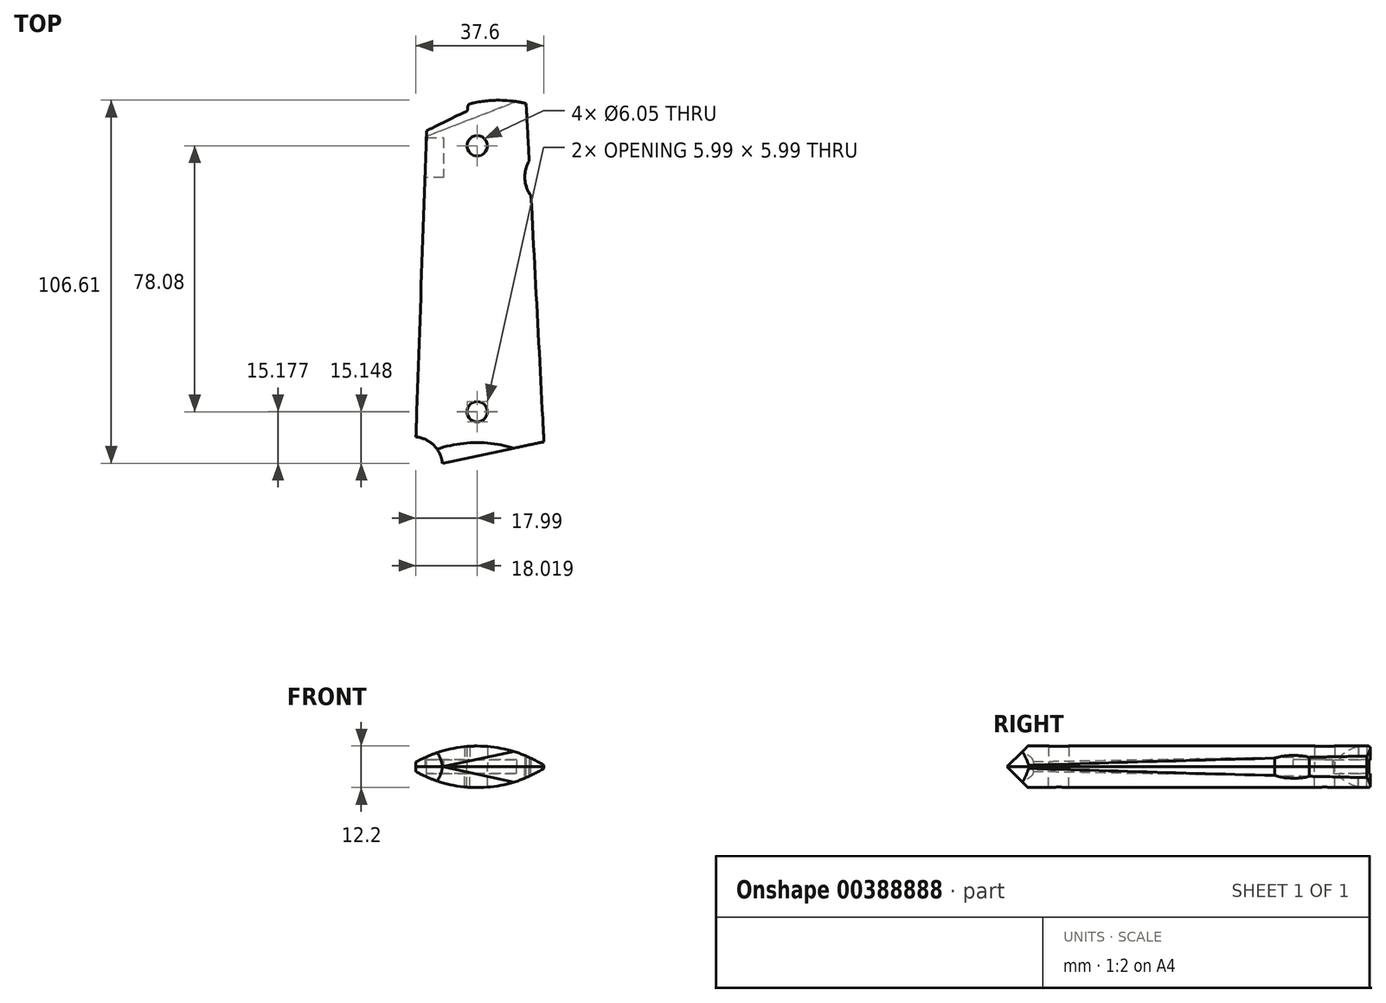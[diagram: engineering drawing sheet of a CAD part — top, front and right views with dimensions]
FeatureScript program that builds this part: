
annotation { "Feature Type Name" : "Feature", "Feature Type Description" : "" }
export const myFeature = defineFeature(function(context is Context, id is Id, definition is map)
    precondition{}
    {
        {
            var Q0;
            Q0=qCreatedBy(makeId("Top.planeOp"),FACE);
            var sketch = newSketch(context, id + "F0", { "sketchPlane" : qUnion([Q0])});
            skCircle(sketch, "E0", {"center": v(0, 44.02) * mm, "radius": 3.02 * mm});
            skCircle(sketch, "E1", {"center": v(0, -34.06) * mm, "radius": 3.02 * mm});
            skArc(sketch, "E2", {"start": v(-10.2, -49.21) * mm, "mid": v(-16.67, -41.7) * mm, "end": v(-25.95, -45.22) * mm});
            skArc(sketch, "E3", {"start": v(15.27, 39.57) * mm, "mid": v(13.98, 34.4) * mm, "end": v(15.8, 29.38) * mm});
            skArc(sketch, "E4", {"start": v(-14.98, 45) * mm, "mid": v(-15, 44.54) * mm, "end": v(-15.01, 44.08) * mm});
            skArc(sketch, "E5", {"start": v(-17.7, -32.88) * mm, "mid": v(-17.72, -33.47) * mm, "end": v(-17.73, -34.06) * mm});
            skLineSegment(sketch, "E6", {"start": v(15.2, 40.98) * mm, "end": v(15.27, 39.57) * mm});
            skLineSegment(sketch, "E7", {"start": v(-15.01, 44.08) * mm, "end": v(-17.73, -34) * mm});
            skLineSegment(sketch, "E8.trimOffspring", {"start": v(15.8, 29.38) * mm, "end": v(19.25, -36.1) * mm});
            skLineSegment(sketch, "E9", {"start": v(19.61, -42.88) * mm, "end": v(-10.2, -49.21) * mm});
            skLineSegment(sketch, "E10", {"start": v(0, -34.06) * mm, "end": v(-82.75, -34.06) * mm, "construction": true});
            skLineSegment(sketch, "E11", {"start": v(19.25, -36.1) * mm, "end": v(19.61, -42.88) * mm});
            skLineSegment(sketch, "E12", {"start": v(-17.73, -34) * mm, "end": v(-17.99, -41.47) * mm});
            skArc(sketch, "E13", {"start": v(14.38, 56.45) * mm, "mid": v(-0.93, 56.62) * mm, "end": v(-14.8, 50.16) * mm});
            skLineSegment(sketch, "E14", {"start": v(15.2, 40.98) * mm, "end": v(14.38, 56.45) * mm});
            skLineSegment(sketch, "E15", {"start": v(-15.01, 44.08) * mm, "end": v(-14.8, 50.16) * mm});
            skSolve(sketch);
        }
        {
            var Q0;
            Q0=makeQuery(id+"F0.imprint","IMPRINT",FACE,{"disambiguationData":[TD([[makeQuery(id+"F0.imprint","IMPRINT",EDGE,{"derivedFrom":sQuery(id+"F0.wireOp",EDGE,"E0")}),-1.0]])]});
            extrude(context, id + "F1", {"entities" : qUnion([Q0]), "depth" : 6.1 * mm});
        }
        {
            var Q0;
            Q0=qCreatedBy(makeId("Front.planeOp"),FACE);
            var sketch = newSketch(context, id + "F2", { "sketchPlane" : qUnion([Q0])});
            skCircle(sketch, "E16", {"center": v(0, -30.73) * mm, "radius": 36.83 * mm});
            skCircle(sketch, "E17", {"center": v(0, -30.73) * mm, "radius": 42.83 * mm});
            skSolve(sketch);
        }
        {
            var Q0;
            Q0=makeQuery(id+"F2.imprint","IMPRINT",FACE,{"disambiguationData":[TD([[makeQuery(id+"F2.imprint","IMPRINT",EDGE,{"derivedFrom":sQuery(id+"F2.wireOp",EDGE,"E16")}),-1.0]])]});
            extrude(context, id + "F3", {"entities" : qUnion([Q0]), "operationType" : NewBodyOperationType.REMOVE, "endBound" : BoundingType.SYMMETRIC, "depth" : 127 * mm});
        }
        {
            var Q0;
            Q0=qCreatedBy(makeId("Right.planeOp"),FACE);
            var sketch = newSketch(context, id + "F4", { "sketchPlane" : qUnion([Q0])});
            skLineSegment(sketch, "E18.0", {"start": v(-49.21, 4.65) * mm, "end": v(-49.21, 0) * mm});
            skLineSegment(sketch, "E18.1", {"start": v(-49.21, 0) * mm, "end": v(-41.47, 0) * mm});
            skLineSegment(sketch, "E19", {"start": v(-41.47, 0) * mm, "end": v(-57, 0) * mm});
            skLineSegment(sketch, "E20", {"start": v(-49.21, 0) * mm, "end": v(-41.47, 7.75) * mm});
            skLineSegment(sketch, "E21", {"start": v(-41.47, 7.75) * mm, "end": v(-52.4, 7.75) * mm});
            skLineSegment(sketch, "E22", {"start": v(-52.4, 7.75) * mm, "end": v(-52.4, 0) * mm});
            skSolve(sketch);
        }
        {
            var Q0;
            {var subQ0=sQuery(id+"F4.wireOp",EDGE,"E20");Q0=makeQuery(id+"F4.imprint","IMPRINT",FACE,{"disambiguationData":[TD([[makeQuery(id+"F4.imprint","IMPRINT",EDGE,{"derivedFrom":subQ0}),1.0]])]});}
            extrude(context, id + "F5", {"entities" : qUnion([Q0]), "operationType" : NewBodyOperationType.REMOVE, "endBound" : BoundingType.SYMMETRIC, "oppositeDirection" : true, "depth" : 76.2 * mm});
        }
        {
            var Q0;
            Q0=qCreatedBy(makeId("Top.planeOp"),FACE);
            var sketch = newSketch(context, id + "F6", { "sketchPlane" : qUnion([Q0])});
            skLineSegment(sketch, "E23", {"start": v(-14.86, 48.44) * mm, "end": v(-14.8, 50.16) * mm});
            skArc(sketch, "E24", {"start": v(-2.14, 56.34) * mm, "mid": v(-2.57, 56) * mm, "end": v(-2.77, 55.49) * mm});
            skLineSegment(sketch, "E25", {"start": v(-2.77, 55.49) * mm, "end": v(-2.85, 54.6) * mm});
            skArc(sketch, "E26", {"start": v(-3.68, 53.93) * mm, "mid": v(-3.12, 54.09) * mm, "end": v(-2.85, 54.6) * mm});
            skLineSegment(sketch, "E27", {"start": v(-3.68, 53.93) * mm, "end": v(-14.86, 48.44) * mm});
            skArc(sketch, "E28", {"start": v(-2.14, 56.34) * mm, "mid": v(-8.78, 53.9) * mm, "end": v(-14.8, 50.16) * mm});
            skLineSegment(sketch, "E29", {"start": v(-2.14, 56.34) * mm, "end": v(-2.14, 57.7) * mm});
            skLineSegment(sketch, "E30", {"start": v(-2.14, 57.7) * mm, "end": v(-16, 52.43) * mm});
            skLineSegment(sketch, "E31", {"start": v(-16, 52.43) * mm, "end": v(-14.86, 48.44) * mm});
            skSolve(sketch);
        }
        {
            var Q0;
            Q0=makeQuery(id+"F6.imprint","IMPRINT",FACE,{"disambiguationData":[TD([[makeQuery(id+"F6.imprint","IMPRINT",EDGE,{"derivedFrom":sQuery(id+"F6.wireOp",EDGE,"E23")}),-1.0]])]});
            var Q1;
            Q1=makeQuery(id+"F6.imprint","IMPRINT",FACE,{"disambiguationData":[TD([[makeQuery(id+"F6.imprint","IMPRINT",EDGE,{"derivedFrom":sQuery(id+"F6.wireOp",EDGE,"E23")}),1.0]])]});
            extrude(context, id + "F7", {"entities" : qUnion([Q0, Q1]), "operationType" : NewBodyOperationType.REMOVE, "depth" : 10.16 * mm});
        }
        {
            var Q0;
            Q0=makeQuery(id+"F1.opExtrude","SWEPT_BODY",BODY,{"disambiguationData":[OSD([sQuery(id+"F0.wireOp",EDGE,"E0"),sQuery(id+"F0.wireOp",EDGE,"E1"),sQuery(id+"F0.wireOp",EDGE,"E2"),sQuery(id+"F0.wireOp",EDGE,"E3"),sQuery(id+"F0.wireOp",EDGE,"E6"),sQuery(id+"F0.wireOp",EDGE,"E7"),sQuery(id+"F0.wireOp",EDGE,"E8.trimOffspring"),sQuery(id+"F0.wireOp",EDGE,"E9"),sQuery(id+"F0.wireOp",EDGE,"E11"),sQuery(id+"F0.wireOp",EDGE,"E12"),sQuery(id+"F0.wireOp",EDGE,"E13"),sQuery(id+"F0.wireOp",EDGE,"E14"),sQuery(id+"F0.wireOp",EDGE,"E15")])]});
            var Q1;
            Q1=qCreatedBy(makeId("Top.planeOp"),FACE);
            mirror(context, id + "F8", {"entities" : qUnion([Q0]), "mirrorPlane" : qUnion([Q1])});
        }
        {
            var Q0;
            Q0=makeQuery(id+"F1.opExtrude","CAP_FACE",FACE,{"disambiguationData":[OSD([sQuery(id+"F0.wireOp",EDGE,"E0"),sQuery(id+"F0.wireOp",EDGE,"E1"),sQuery(id+"F0.wireOp",EDGE,"E2"),sQuery(id+"F0.wireOp",EDGE,"E3"),sQuery(id+"F0.wireOp",EDGE,"E6"),sQuery(id+"F0.wireOp",EDGE,"E7"),sQuery(id+"F0.wireOp",EDGE,"E8.trimOffspring"),sQuery(id+"F0.wireOp",EDGE,"E9"),sQuery(id+"F0.wireOp",EDGE,"E11"),sQuery(id+"F0.wireOp",EDGE,"E12"),sQuery(id+"F0.wireOp",EDGE,"E13"),sQuery(id+"F0.wireOp",EDGE,"E14"),sQuery(id+"F0.wireOp",EDGE,"E15")])],"isStart":true});
            var sketch = newSketch(context, id + "F9", { "sketchPlane" : qUnion([Q0])});
            skLineSegment(sketch, "E32", {"start": v(-14.93, -46.4) * mm, "end": v(-9.85, -46.4) * mm});
            skLineSegment(sketch, "E33", {"start": v(-9.85, -46.4) * mm, "end": v(-9.85, -34.73) * mm});
            skLineSegment(sketch, "E34", {"start": v(-9.85, -34.73) * mm, "end": v(-15.34, -34.73) * mm});
            skLineSegment(sketch, "E35", {"start": v(-15.34, -34.73) * mm, "end": v(-14.93, -46.4) * mm});
            skPoint(sketch, "E36.0", {"position": v(-14.86, -48.44) * mm});
            skSolve(sketch);
        }
        {
            var Q0;
            Q0=makeQuery(id+"F9.imprint","IMPRINT",FACE,{"disambiguationData":[TD([[makeQuery(id+"F9.imprint","IMPRINT",EDGE,{"derivedFrom":sQuery(id+"F9.wireOp",EDGE,"E32")}),1.0]])]});
            extrude(context, id + "F10", {"entities" : qUnion([Q0]), "operationType" : NewBodyOperationType.REMOVE, "oppositeDirection" : true, "depth" : 2.13 * mm});
        }
        {
            var Q0;
            Q0=makeQuery(id+"F8.opPattern","COPY",FACE,{"derivedFrom":makeQuery(id+"F1.opExtrude","CAP_FACE",FACE,{"disambiguationData":[OSD([sQuery(id+"F0.wireOp",EDGE,"E0"),sQuery(id+"F0.wireOp",EDGE,"E1"),sQuery(id+"F0.wireOp",EDGE,"E2"),sQuery(id+"F0.wireOp",EDGE,"E3"),sQuery(id+"F0.wireOp",EDGE,"E6"),sQuery(id+"F0.wireOp",EDGE,"E7"),sQuery(id+"F0.wireOp",EDGE,"E8.trimOffspring"),sQuery(id+"F0.wireOp",EDGE,"E9"),sQuery(id+"F0.wireOp",EDGE,"E11"),sQuery(id+"F0.wireOp",EDGE,"E12"),sQuery(id+"F0.wireOp",EDGE,"E13"),sQuery(id+"F0.wireOp",EDGE,"E14"),sQuery(id+"F0.wireOp",EDGE,"E15")])],"isStart":true}),"instanceName":"1"});
            var sketch = newSketch(context, id + "F11", { "sketchPlane" : qUnion([Q0])});
            skCircle(sketch, "E37.0", {"center": v(0, 44.02) * mm, "radius": 3.02 * mm});
            skLineSegment(sketch, "E38", {"start": v(-22.15, 44.02) * mm, "end": v(23.77, 44.08) * mm, "construction": true});
            skLineSegment(sketch, "E39", {"start": v(-22.15, 44.02) * mm, "end": v(12.38, 57.33) * mm});
            skLineSegment(sketch, "E40", {"start": v(-22.15, 44.02) * mm, "end": v(-22.19, 68.44) * mm});
            skLineSegment(sketch, "E41", {"start": v(-22.19, 68.44) * mm, "end": v(12.38, 57.33) * mm});
            skSolve(sketch);
        }
        {
            var Q0;
            Q0=makeQuery(id+"F11.imprint","IMPRINT",FACE,{"disambiguationData":[TD([[makeQuery(id+"F11.imprint","IMPRINT",EDGE,{"derivedFrom":makeQuery(id+"F8.opPattern","COPY",EDGE,{"derivedFrom":makeQuery(id+"Fb7e4hwDuQcyxQq_1.boolean.opBoolean","COPY",EDGE,{"derivedFrom":makeQuery(id+"Fb7e4hwDuQcyxQq_1.opExtrude","CAP_EDGE",EDGE,{"disambiguationData":[OSD([sQuery(id+"FKYqYQtcE7hS676_1.wireOp",EDGE,"TWVttyq0-dFbJ-dXUh-rKFH-anJvTX5drRZ4")])],"isStart":true})}),"instanceName":"1"})}),1.0]])]});
            var Q1;
            {var subQ1=sQuery(id+"F11.wireOp",EDGE,"E40");Q1=makeQuery(id+"F11.imprint","IMPRINT",FACE,{"disambiguationData":[TD([[makeQuery(id+"F11.imprint","IMPRINT",EDGE,{"derivedFrom":subQ1}),-1.0]])]});}
            var Q2;
            {var subQ0=sQuery(id+"F11.wireOp",EDGE,"E39");var subQ1=makeQuery(id+"F8.opPattern","COPY",EDGE,{"derivedFrom":makeQuery(id+"F1.opExtrude","CAP_EDGE",EDGE,{"disambiguationData":[OSD([sQuery(id+"F0.wireOp",EDGE,"E15")])],"isStart":true}),"instanceName":"1"});var subQ2=makeQuery(id+"F11.imprint","INTERSECT",VERTEX,{"derivedFrom":[subQ1,subQ0]});Q2=makeQuery(id+"F11.imprint","IMPRINT",FACE,{"disambiguationData":[TD([[makeQuery(id+"F11.imprint","IMPRINT",EDGE,{"disambiguationData":[TD([[subQ2,-1.0]])],"derivedFrom":subQ0}),1.0]])]});}
            extrude(context, id + "F12", {"entities" : qUnion([Q0, Q1, Q2]), "operationType" : NewBodyOperationType.REMOVE, "endBound" : BoundingType.SYMMETRIC, "oppositeDirection" : true, "depth" : 4.06 * mm});
        }
    });
